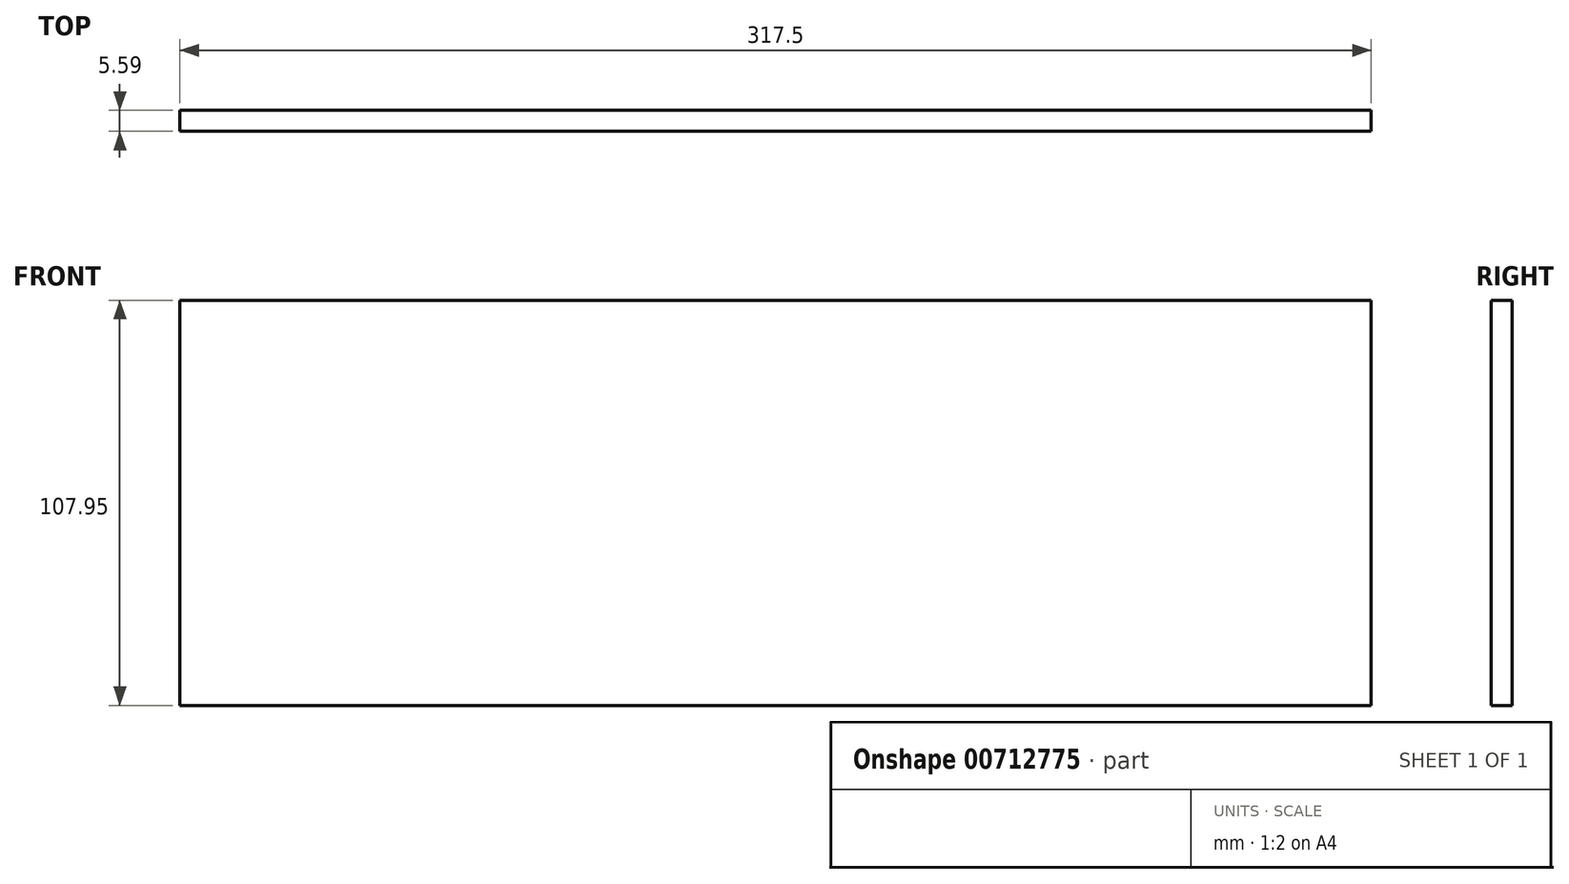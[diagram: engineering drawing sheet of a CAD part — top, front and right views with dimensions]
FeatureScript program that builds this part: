
annotation { "Feature Type Name" : "Feature", "Feature Type Description" : "" }
export const myFeature = defineFeature(function(context is Context, id is Id, definition is map)
    precondition{}
    {
        {
            var Q0;
            Q0=qCreatedBy(makeId("Front.planeOp"),FACE);
            var sketch = newSketch(context, id + "F0", { "sketchPlane" : qUnion([Q0])});
            skLineSegment(sketch, "E0.bottom", {"start": v(0, 0) * mm, "end": v(-317.5, 0) * mm});
            skLineSegment(sketch, "E0.top", {"start": v(0, 107.95) * mm, "end": v(-317.5, 107.95) * mm});
            skLineSegment(sketch, "E0.left", {"start": v(0, 0) * mm, "end": v(0, 107.95) * mm});
            skLineSegment(sketch, "E0.right", {"start": v(-317.5, 0) * mm, "end": v(-317.5, 107.95) * mm});
            skSolve(sketch);
        }
        {
            var Q0;
            Q0 = qSketchRegion(id + "F0", true);
            extrude(context, id + "F1", {"entities" : qUnion([Q0]), "depth" : 5.6 * mm, "offsetDistance" : 25.4 * mm});
        }
    });
